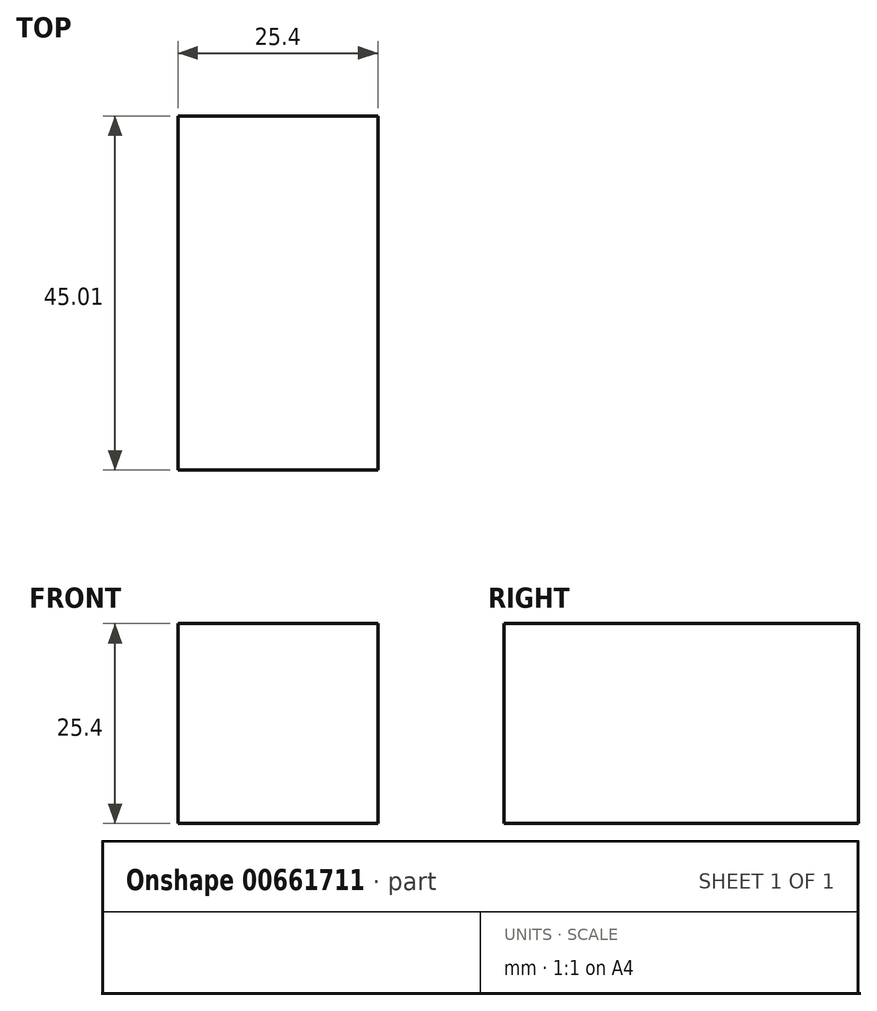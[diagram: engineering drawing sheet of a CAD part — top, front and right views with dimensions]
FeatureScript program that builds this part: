
annotation { "Feature Type Name" : "Feature", "Feature Type Description" : "" }
export const myFeature = defineFeature(function(context is Context, id is Id, definition is map)
    precondition{}
    {
        {
            var Q0;
            Q0=qCreatedBy(makeId("Top.planeOp"),FACE);
            var sketch = newSketch(context, id + "F0", { "sketchPlane" : qUnion([Q0])});
            skLineSegment(sketch, "E0.bottom", {"start": v(0, 0) * mm, "end": v(25.4, 0) * mm});
            skLineSegment(sketch, "E0.top", {"start": v(0, 45) * mm, "end": v(25.4, 45) * mm});
            skLineSegment(sketch, "E0.left", {"start": v(0, 0) * mm, "end": v(0, 45) * mm});
            skLineSegment(sketch, "E0.right", {"start": v(25.4, 0) * mm, "end": v(25.4, 45) * mm});
            skSolve(sketch);
        }
        {
            var Q0;
            Q0=makeQuery(id+"F0.imprint","IMPRINT",FACE,{"disambiguationData":[TD([[makeQuery(id+"F0.imprint","IMPRINT",EDGE,{"derivedFrom":sQuery(id+"F0.wireOp",EDGE,"E0.bottom")}),1.0]])]});
            extrude(context, id + "F1", {"entities" : qUnion([Q0]), "depth" : 25.4 * mm, "offsetDistance" : 25.4 * mm});
        }
    });
